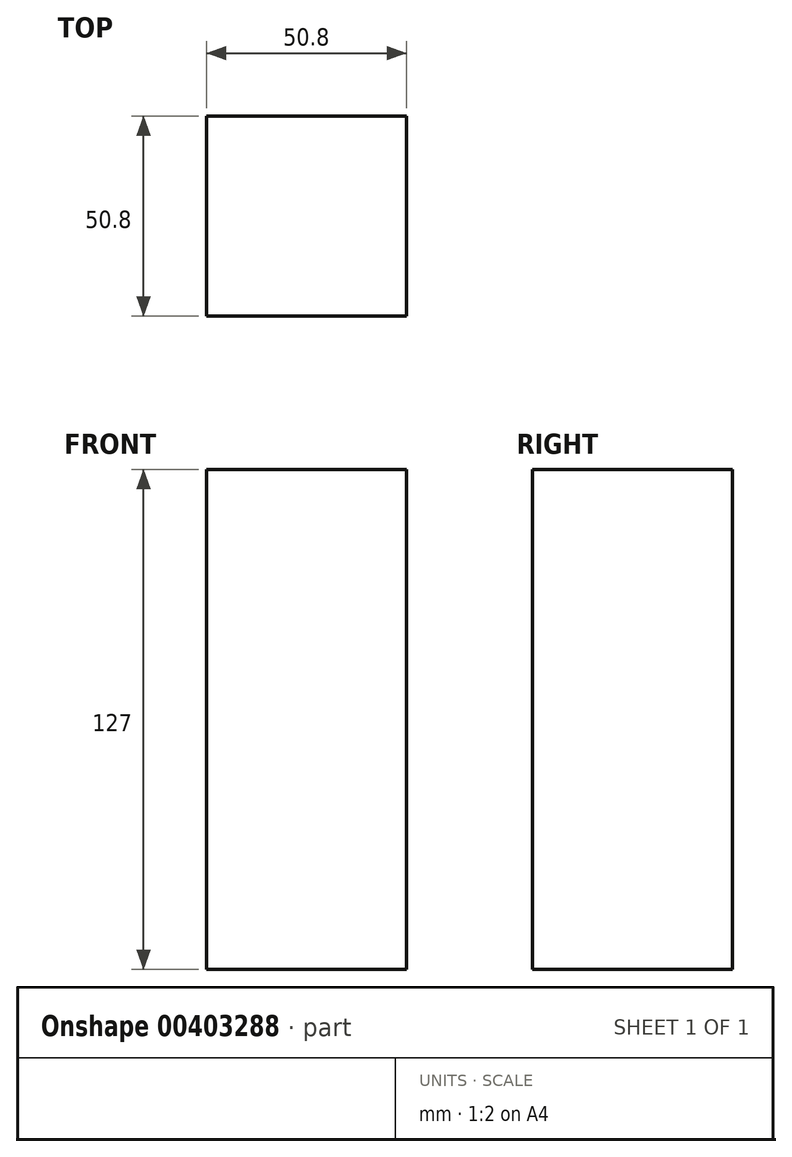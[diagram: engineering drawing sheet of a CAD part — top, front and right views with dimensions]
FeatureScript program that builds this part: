
annotation { "Feature Type Name" : "Feature", "Feature Type Description" : "" }
export const myFeature = defineFeature(function(context is Context, id is Id, definition is map)
    precondition{}
    {
        {
            var Q0;
            Q0=qCreatedBy(makeId("Top.planeOp"),FACE);
            var sketch = newSketch(context, id + "F0", { "sketchPlane" : qUnion([Q0])});
            skLineSegment(sketch, "E0.bottom", {"start": v(0, 0) * mm, "end": v(50.8, 0) * mm});
            skLineSegment(sketch, "E0.top", {"start": v(0, 50.8) * mm, "end": v(50.8, 50.8) * mm});
            skLineSegment(sketch, "E0.left", {"start": v(0, 0) * mm, "end": v(0, 50.8) * mm});
            skLineSegment(sketch, "E0.right", {"start": v(50.8, 0) * mm, "end": v(50.8, 50.8) * mm});
            skSolve(sketch);
        }
        {
            var Q0;
            Q0 = qSketchRegion(id + "F0", true);
            extrude(context, id + "F1", {"entities" : qUnion([Q0]), "depth" : 127 * mm});
        }
    });
